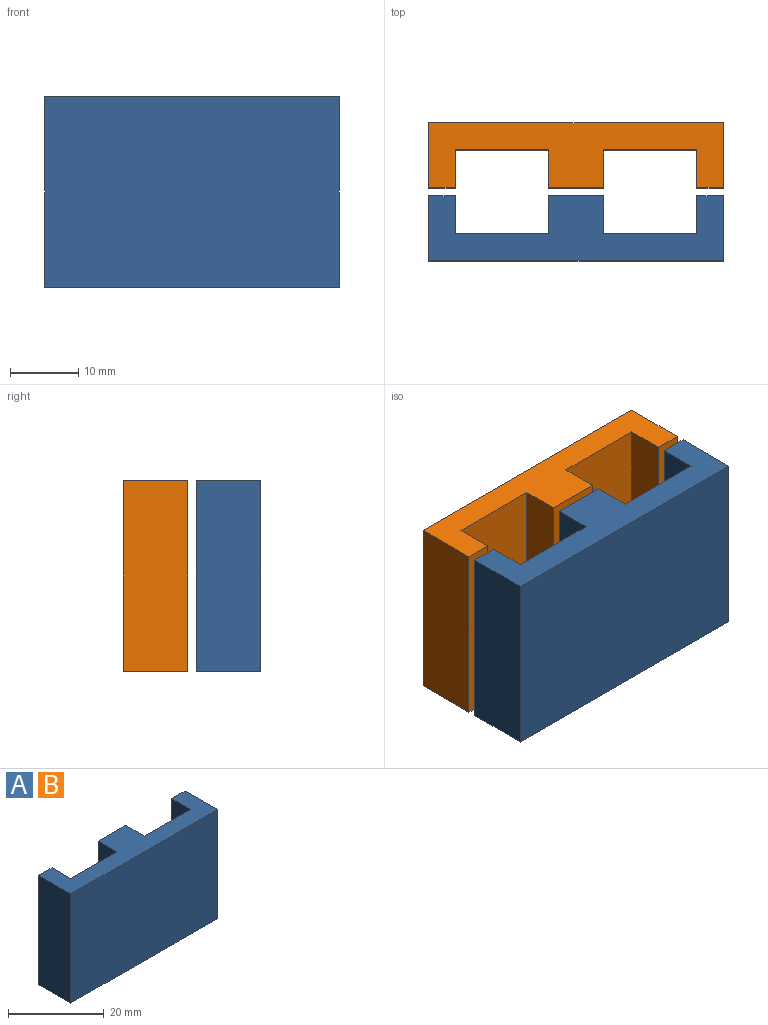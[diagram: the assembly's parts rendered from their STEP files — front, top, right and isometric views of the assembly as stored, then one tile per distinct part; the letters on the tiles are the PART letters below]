
ASSEMBLY  parts=2 mates=1
PART A: 14 faces, bbox 43.2x9.5x27.9 mm
  f0: plane 27.9x3.9mm, normal (0,1,0), area 108.8mm2, adj f1,f11,f12,f13
  f1: plane 27.9x9.5mm, normal (-1,0,0), area 265.1mm2, adj f0,f2,f12,f13
  f2: plane 43.21x27.9mm, normal (0,-1,0), area 1205.5mm2, adj f1,f3,f12,f13
  f3: plane 27.9x9.5mm, normal (1,0,0), area 265mm2, adj f2,f4,f12,f13
  f4: plane 27.9x3.9mm, normal (0,1,0), area 108.8mm2, adj f3,f5,f12,f13
  f5: plane 27.9x5.55mm, normal (-1,0,0), area 154.7mm2, adj f4,f6,f12,f13
  f6: plane 27.9x13.65mm, normal (0,1,0), area 380.8mm2, adj f5,f7,f12,f13
  f7: plane 27.9x5.55mm, normal (1,0,0), area 154.7mm2, adj f6,f8,f12,f13
  f8: plane 27.9x8.1mm, normal (0,1,0), area 226mm2, adj f7,f9,f12,f13
  f9: plane 27.9x5.55mm, normal (-1,0,0), area 154.7mm2, adj f8,f10,f12,f13
  f10: plane 27.9x13.65mm, normal (0,1,0), area 380.8mm2, adj f9,f11,f12,f13
  f11: plane 27.9x5.55mm, normal (1,0,0), area 154.7mm2, adj f0,f10,f12,f13
  f12: plane 43.21x9.5mm, normal (0,0,-1), area 259mm2, adj f0,f1,f2,f3,f4,f5,f6,f7
  f13: plane 43.21x9.5mm, normal (0,0,1), area 259mm2, adj f0,f1,f2,f3,f4,f5,f6,f7
PART B: same geometry as A
PLACE A t=(-1.7,4.22,0.68)mm
PLACE B rot(axis=(0,0,1),180deg) t=(-1.71,5.4,0.68)mm
MATE fastened B.f13 <-> A.f13  axis (0,0,1) through (-1.71,11.31,14.63)mm
